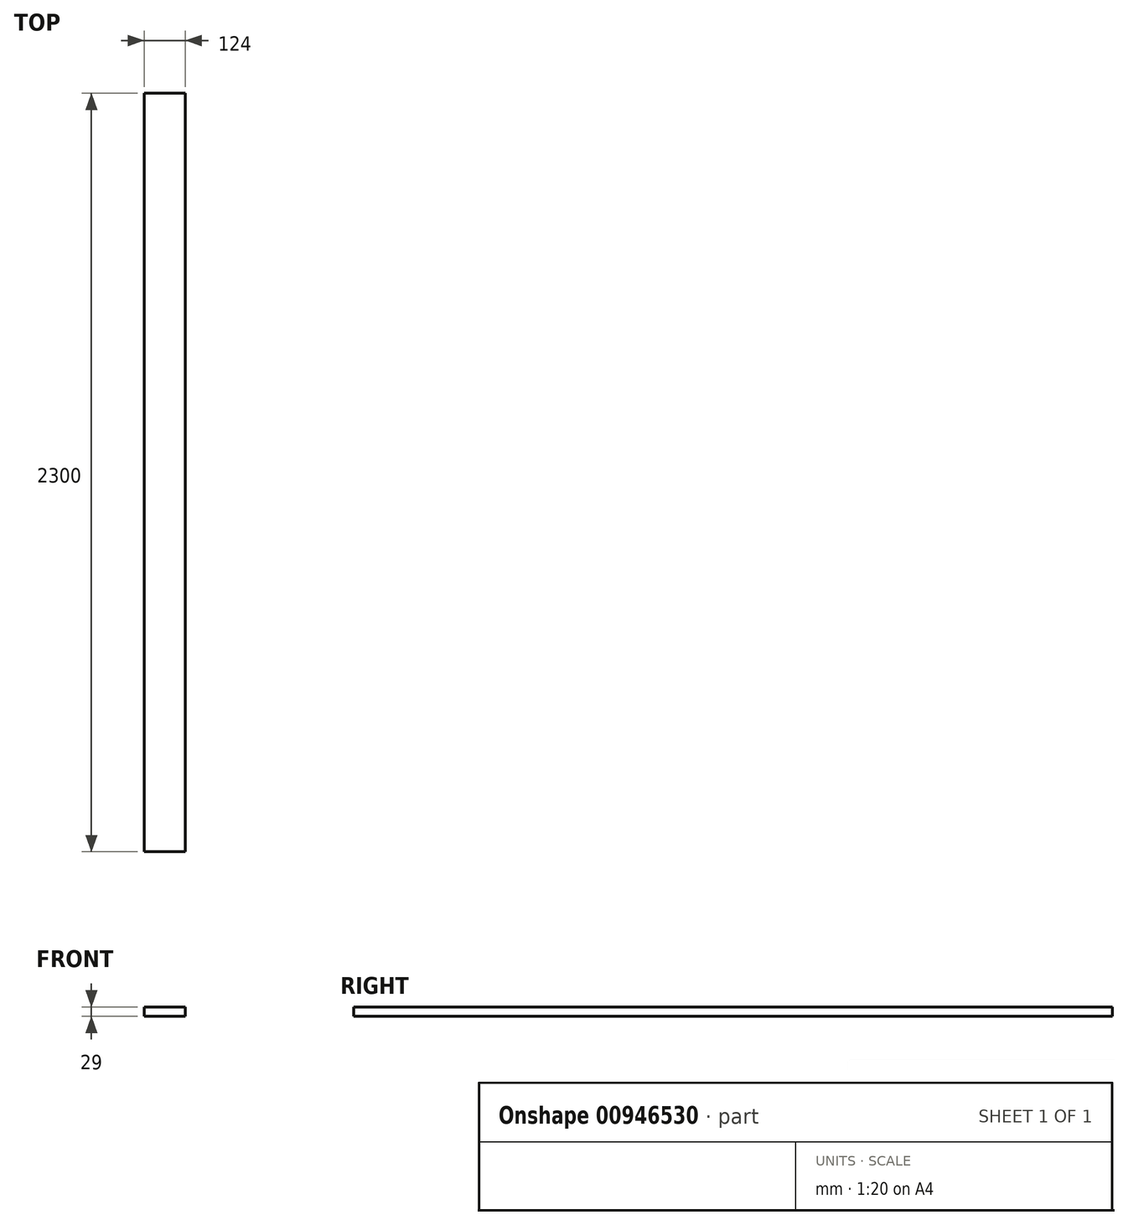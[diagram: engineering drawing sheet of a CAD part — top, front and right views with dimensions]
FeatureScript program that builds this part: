
annotation { "Feature Type Name" : "Feature", "Feature Type Description" : "" }
export const myFeature = defineFeature(function(context is Context, id is Id, definition is map)
    precondition{}
    {
        {
            var Q0;
            Q0=qCreatedBy(makeId("Front.planeOp"),FACE);
            var sketch = newSketch(context, id + "F0", { "sketchPlane" : qUnion([Q0])});
            skLineSegment(sketch, "E0.bottom", {"start": v(0, 0) * mm, "end": v(124, 0) * mm});
            skLineSegment(sketch, "E0.top", {"start": v(0, 29) * mm, "end": v(124, 29) * mm});
            skLineSegment(sketch, "E0.left", {"start": v(0, 0) * mm, "end": v(0, 29) * mm});
            skLineSegment(sketch, "E0.right", {"start": v(124, 0) * mm, "end": v(124, 29) * mm});
            skSolve(sketch);
        }
        {
            var Q0;
            Q0=qSketchRegion(id+"F0",true);
            extrude(context, id + "F1", {"entities" : qUnion([Q0]), "depth" : 2300 * mm, "offsetDistance" : 25 * mm});
        }
    });
